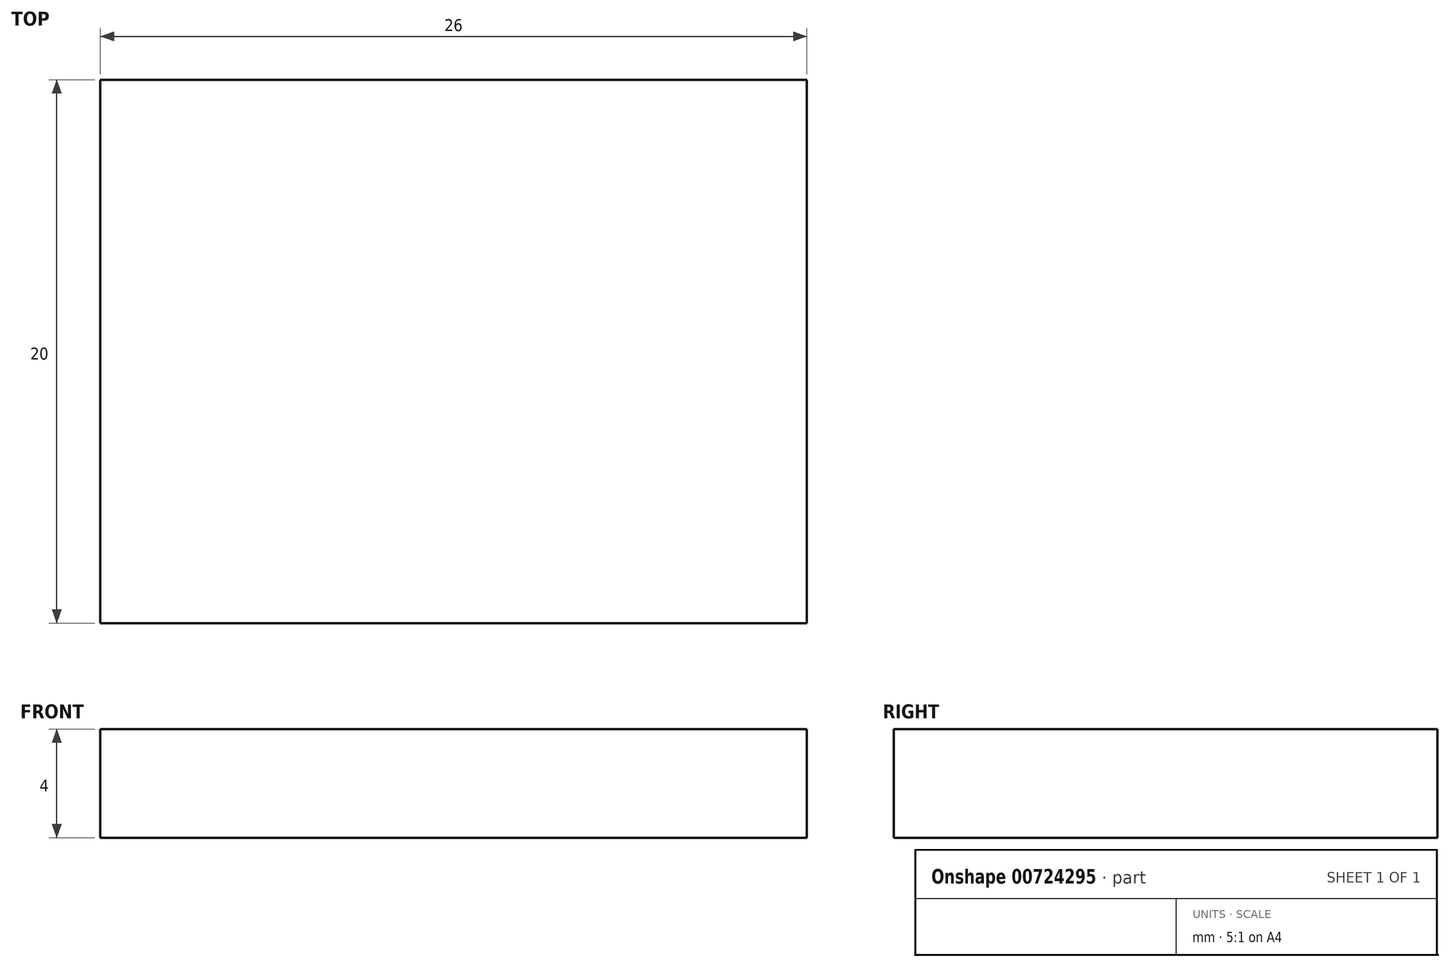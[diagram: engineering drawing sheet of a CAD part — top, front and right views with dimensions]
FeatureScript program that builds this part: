
annotation { "Feature Type Name" : "Feature", "Feature Type Description" : "" }
export const myFeature = defineFeature(function(context is Context, id is Id, definition is map)
    precondition{}
    {
        {
            var Q0;
            Q0=qCreatedBy(makeId("Top.planeOp"),FACE);
            var sketch = newSketch(context, id + "F0", { "sketchPlane" : qUnion([Q0])});
            skLineSegment(sketch, "E0.bottom", {"start": v(-34.91, 30.39) * mm, "end": v(-8.91, 30.39) * mm});
            skLineSegment(sketch, "E0.top", {"start": v(-34.91, 10.39) * mm, "end": v(-8.91, 10.39) * mm});
            skLineSegment(sketch, "E0.left", {"start": v(-34.91, 30.39) * mm, "end": v(-34.91, 10.39) * mm});
            skLineSegment(sketch, "E0.right", {"start": v(-8.91, 30.39) * mm, "end": v(-8.91, 10.39) * mm});
            skSolve(sketch);
        }
        {
            var Q0;
            Q0=qSketchRegion(id+"F0",true);
            extrude(context, id + "F1", {"entities" : qUnion([Q0]), "depth" : 4 * mm, "offsetDistance" : 25 * mm});
        }
    });
